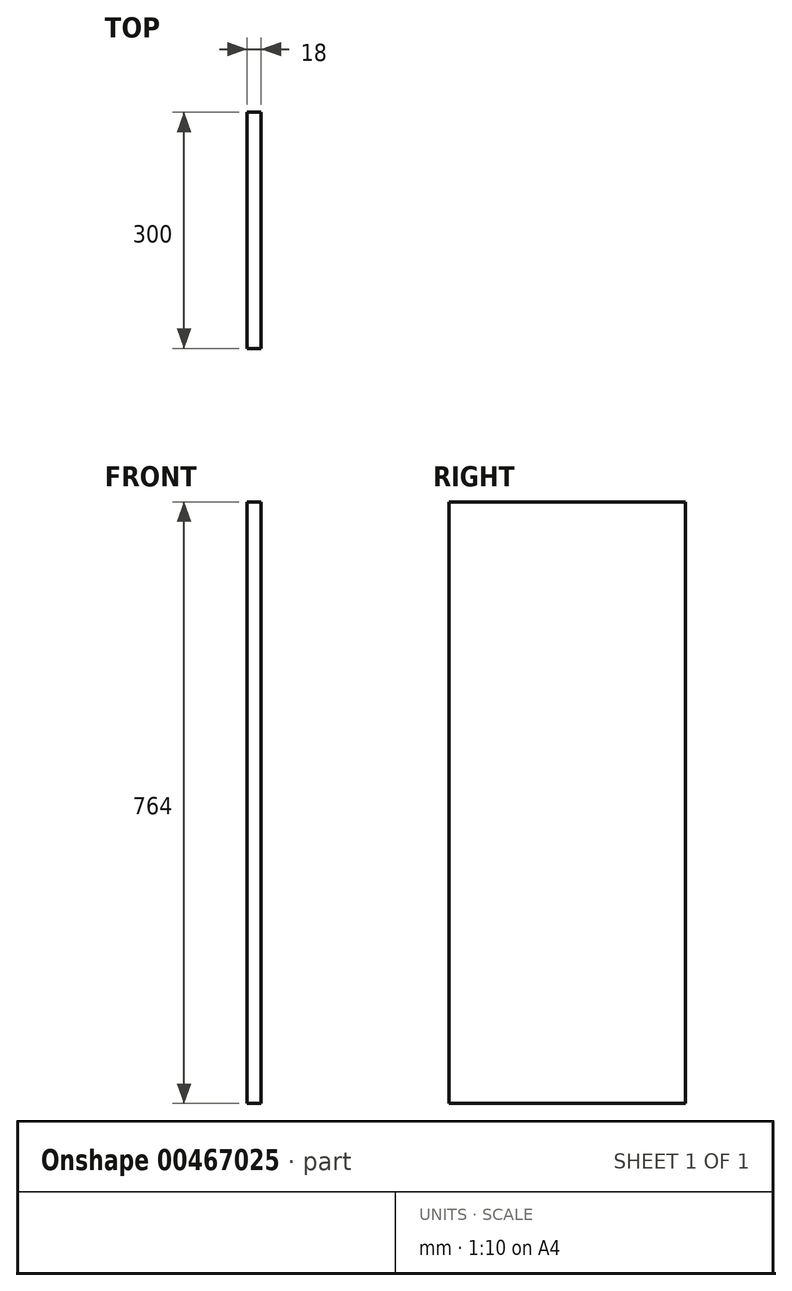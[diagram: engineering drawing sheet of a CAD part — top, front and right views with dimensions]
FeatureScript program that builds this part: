
annotation { "Feature Type Name" : "Feature", "Feature Type Description" : "" }
export const myFeature = defineFeature(function(context is Context, id is Id, definition is map)
    precondition{}
    {
        {
            var Q0;
            Q0=qCreatedBy(makeId("Right.planeOp"),FACE);
            var sketch = newSketch(context, id + "F0", { "sketchPlane" : qUnion([Q0])});
            skLineSegment(sketch, "E0.bottom", {"start": v(0, 0) * mm, "end": v(300, 0) * mm});
            skLineSegment(sketch, "E0.top", {"start": v(0, 764) * mm, "end": v(300, 764) * mm});
            skLineSegment(sketch, "E0.left", {"start": v(0, 0) * mm, "end": v(0, 764) * mm});
            skLineSegment(sketch, "E0.right", {"start": v(300, 0) * mm, "end": v(300, 764) * mm});
            skSolve(sketch);
        }
        {
            var Q0;
            Q0 = qSketchRegion(id + "F0", true);
            extrude(context, id + "F1", {"entities" : qUnion([Q0]), "depth" : 18 * mm, "offsetDistance" : 25 * mm});
        }
    });
